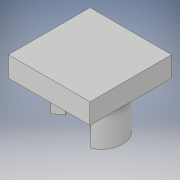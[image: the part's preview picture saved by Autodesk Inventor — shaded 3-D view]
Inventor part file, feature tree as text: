
AUTODESK INVENTOR PART (.ipt)
format: ipt  version: 2019 (Build 230136000, 136)  size: 121,344 bytes
history: native  units: mm
features: extrude x2, sketch x1
ambient origin geometry x8: Origin, YZ Plane, XZ Plane, XY Plane, X Axis, Y Axis, Z Axis, Center Point
bodies: Solid1 (feature_tree)
feature tree (3):
  sketch  "Sketch1"  dims[d0=20.0mm d1=20.0mm d2=2.5mm d3=2.5mm d4=2.5mm d6=1.5mm d7=11.34464mm d8=6.108652mm d9=2.5mm d10=2.5mm d11=10.0mm d12=0.0mm d13=5.0mm d14=0.0mm]
  extrude  "Extrusion1"  Depth=20.0mm
  extrude  "Extrusion2"  Depth=5.0mm
